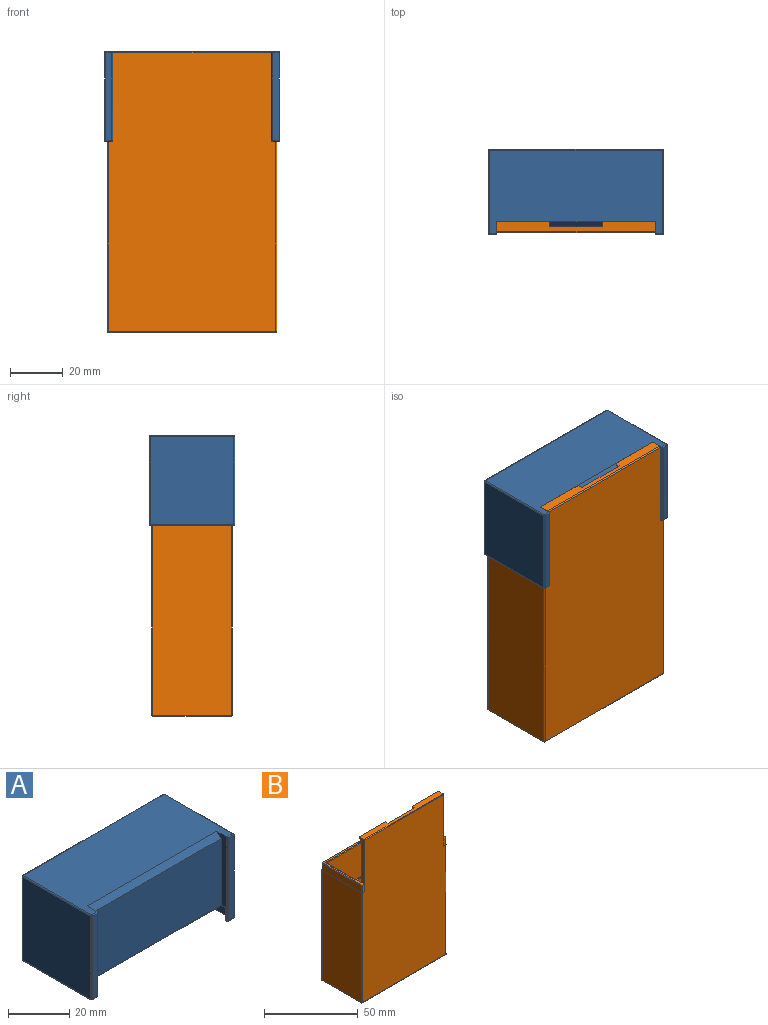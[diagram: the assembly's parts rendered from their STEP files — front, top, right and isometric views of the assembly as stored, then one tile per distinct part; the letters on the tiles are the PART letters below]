
ASSEMBLY  parts=2 mates=1
PART A: 63 faces, bbox 66x32.4x34 mm
  f0: plane 26.6x23mm, normal (1,0,0), area 611.8mm2, adj f1,f6,f19,f60
  f1: plane 60x26.6mm, normal (0,-1,0), area 1596mm2, adj f0,f2,f19,f59
  f2: plane 26.6x23mm, normal (-1,0,0), area 611.8mm2, adj f1,f6,f19,f61
  f3: plane 33.6x4.6mm, normal (1,0,0), area 77.4mm2, adj f4,f20,f21,f39,f43,f51,f57
  f4: plane 60x26.6mm, normal (0,-1,0), area 1596mm2, adj f3,f5,f21,f34
  f5: plane 33.6x4.6mm, normal (-1,0,0), area 77.4mm2, adj f4,f20,f21,f22,f26,f29,f30
  f6: plane 60x26.6mm, normal (0,1,0), area 1596mm2, adj f0,f2,f19,f62
  f7: plane 64x30.4mm, normal (0,0,-1), area 352.6mm2, adj f8,f9,f10,f11,f12,f30,f34,f39
  f8: plane 30.4x4.6mm, normal (-1,0,0), area 139.8mm2, adj f7,f9,f12,f31
  f9: plane 64x4.6mm, normal (0,-1,0), area 294.4mm2, adj f7,f8,f10,f35
  f10: plane 30.4x4.6mm, normal (1,0,0), area 139.8mm2, adj f7,f9,f11,f40
  f11: plane 4.6x1.6mm, normal (0,1,0), area 7.4mm2, adj f7,f10,f43,f44
  f12: plane 4.6x1.6mm, normal (0,1,0), area 7.4mm2, adj f7,f8,f26,f27
  f13: plane 33.2x2.6mm, normal (0,-1,0), area 86.3mm2, adj f14,f24,f29,f33
  f14: plane 33.2x32mm, normal (1,0,0), area 1062.4mm2, adj f13,f28,f37,f38
  f15: plane 65.2x33.2mm, normal (0,1,0), area 2164.6mm2, adj f36,f37,f46,f47
  f16: plane 33.2x31.6mm, normal (-1,0,0), area 1049.1mm2, adj f45,f46,f53,f54
  f17: plane 33.2x2.2mm, normal (0,-1,0), area 73mm2, adj f52,f53,f57,f58
  f18: plane 65.2x31.6mm, normal (0,0,-1), area 26.4mm2, adj f22,f24,f27,f28,f31,f35,f36,f40
  f19: plane 60x23mm, normal (0,0,-1), area 1380mm2, adj f0,f1,f2,f6
  f20: plane 65.2x31.6mm, normal (0,0,1), area 1784.3mm2, adj f3,f5,f21,f33,f38,f47,f54,f58
  f21: plane 60x2mm, normal (0,-0.71,0.71), area 169.7mm2, adj f3,f4,f5,f20
  f22: cylinder r=0.4mm len=0.4mm, axis (0,1,0), area 0.1mm2, adj f5,f18,f23,f25
  f23: sphere r=0.4mm, area 0.3mm2, adj f22,f26,f27
  f24: cylinder r=0.4mm len=2.6mm, axis (-1,0,0), area 1.5mm2, adj f13,f18,f25,f28
  f25: sphere r=0.4mm, area 0.3mm2, adj f22,f24,f29
  f26: cylinder r=0.4mm len=5mm, axis (0,0,1), area 3mm2, adj f5,f12,f23,f30
  f27: cylinder r=0.4mm len=2mm, axis (1,0,0), area 1.1mm2, adj f12,f18,f23,f31
  f28: cylinder r=0.4mm len=32mm, axis (0,-1,0), area 20mm2, adj f14,f18,f24,f32
  f29: cylinder r=0.4mm len=33.6mm, axis (0,0,-1), area 21mm2, adj f5,f13,f25,f33
  f30: cylinder r=0.4mm len=2.8mm, axis (0,1,0), area 1.4mm2, adj f5,f7,f26,f34
  f31: cylinder r=0.4mm len=31.2mm, axis (0,1,0), area 19.3mm2, adj f8,f18,f27,f35
  f32: sphere r=0.4mm, area 0.3mm2, adj f28,f36,f37
  f33: cylinder r=0.4mm len=3mm, axis (1,0,0), area 1.7mm2, adj f13,f20,f29,f38
  f34: cylinder r=0.4mm len=60.8mm, axis (-1,0,0), area 37.9mm2, adj f4,f7,f30,f39
  f35: cylinder r=0.4mm len=64.8mm, axis (-1,0,0), area 40.4mm2, adj f9,f18,f31,f40
  f36: cylinder r=0.4mm len=65.2mm, axis (1,0,0), area 41mm2, adj f15,f18,f32,f41
  f37: cylinder r=0.4mm len=33.2mm, axis (0,0,1), area 20.9mm2, adj f14,f15,f32,f42
  f38: cylinder r=0.4mm len=32mm, axis (0,1,0), area 20mm2, adj f14,f20,f33,f42
  f39: cylinder r=0.4mm len=2.8mm, axis (0,-1,0), area 1.4mm2, adj f3,f7,f34,f43
  f40: cylinder r=0.4mm len=31.2mm, axis (0,-1,0), area 19.3mm2, adj f10,f18,f35,f44
  f41: sphere r=0.4mm, area 0.3mm2, adj f36,f45,f46
  f42: sphere r=0.4mm, area 0.3mm2, adj f37,f38,f47
  f43: cylinder r=0.4mm len=5mm, axis (0,0,1), area 3mm2, adj f3,f11,f39,f48
  f44: cylinder r=0.4mm len=2mm, axis (1,0,0), area 1.1mm2, adj f11,f18,f40,f48
  f45: cylinder r=0.4mm len=31.6mm, axis (0,1,0), area 19.9mm2, adj f16,f18,f41,f49
  f46: cylinder r=0.4mm len=33.2mm, axis (0,0,-1), area 20.9mm2, adj f15,f16,f41,f50
  f47: cylinder r=0.4mm len=65.2mm, axis (-1,0,0), area 41mm2, adj f15,f20,f42,f50
  f48: sphere r=0.4mm, area 0.3mm2, adj f43,f44,f51
  f49: sphere r=0.4mm, area 0.3mm2, adj f45,f52,f53
  f50: sphere r=0.4mm, area 0.3mm2, adj f46,f47,f54
  f51: cylinder r=0.4mm len=0.4mm, axis (0,-1,0), area 0.1mm2, adj f3,f18,f48,f55
  f52: cylinder r=0.4mm len=2.2mm, axis (-1,0,0), area 1.4mm2, adj f17,f18,f49,f55
  f53: cylinder r=0.4mm len=33.2mm, axis (0,0,1), area 20.9mm2, adj f16,f17,f49,f56
  f54: cylinder r=0.4mm len=31.6mm, axis (0,-1,0), area 19.9mm2, adj f16,f20,f50,f56
  f55: sphere r=0.4mm, area 0.3mm2, adj f51,f52,f57
  f56: sphere r=0.4mm, area 0.3mm2, adj f53,f54,f58
  f57: cylinder r=0.4mm len=33.6mm, axis (0,0,-1), area 21mm2, adj f3,f17,f55,f58
  f58: cylinder r=0.4mm len=2.6mm, axis (1,0,0), area 1.5mm2, adj f17,f20,f56,f57
  f59: cylinder r=0.4mm len=60.8mm, axis (-1,0,0), area 37.9mm2, adj f1,f7,f60,f61
  f60: cylinder r=0.4mm len=23.8mm, axis (0,-1,0), area 14.6mm2, adj f0,f7,f59,f62
  f61: cylinder r=0.4mm len=23.8mm, axis (0,1,0), area 14.6mm2, adj f2,f7,f59,f62
  f62: cylinder r=0.4mm len=60.8mm, axis (1,0,0), area 37.9mm2, adj f6,f7,f60,f61
PART B: 61 faces, bbox 64x30.4x106 mm
  f0: plane 63x29.4mm, normal (0,0,1), area 172mm2, adj f7,f8,f13,f19,f20,f32,f35,f38
  f1: plane 105.2x63.2mm, normal (0,-1,0), area 6541.1mm2, adj f19,f20,f28,f44,f47,f52,f53
  f2: plane 29.4x4.6mm, normal (-1,0,0), area 135.2mm2, adj f28,f37,f40,f43
  f3: plane 29.4x4.6mm, normal (1,0,0), area 135.2mm2, adj f28,f31,f34,f35
  f4: plane 63x4.6mm, normal (0,1,0), area 289.8mm2, adj f28,f34,f37,f38
  f5: plane 71.6x29.6mm, normal (-1,0,0), area 2119.4mm2, adj f28,f45,f46,f47
  f6: plane 104x60mm, normal (0,1,0), area 6055mm2, adj f7,f8,f9,f19,f20,f21,f22,f23
  f7: plane 68x3.4mm, normal (1,0,0), area 231.2mm2, adj f0,f6,f13,f27
  f8: plane 68x3.4mm, normal (-1,0,0), area 231.2mm2, adj f0,f6,f13,f26
  f9: plane 30x3.4mm, normal (0,0,1), area 102mm2, adj f6,f13,f26,f27
  f10: plane 74.6x60mm, normal (0,1,0), area 4476mm2, adj f11,f16,f17,f59
  f11: plane 74.6x22mm, normal (1,0,0), area 1641.2mm2, adj f10,f12,f17,f57
  f12: plane 74.6x60mm, normal (0,-1,0), area 4476mm2, adj f11,f16,f17,f58
  f13: plane 75x60mm, normal (0,-1,0), area 4395mm2, adj f0,f7,f8,f9,f26,f27
  f14: plane 71.6x29.6mm, normal (1,0,0), area 2119.4mm2, adj f28,f50,f53,f56
  f15: plane 71.6x63.2mm, normal (0,1,0), area 4525.1mm2, adj f28,f45,f50,f51
  f16: plane 74.6x22mm, normal (-1,0,0), area 1641.2mm2, adj f10,f12,f17,f60
  f17: plane 60x22mm, normal (0,0,1), area 1320mm2, adj f10,f11,f12,f16
  f18: plane 63.2x29.6mm, normal (0,0,-1), area 1870.7mm2, adj f46,f51,f52,f56
  f19: plane 34x4mm, normal (-1,0,0), area 60.5mm2, adj f0,f1,f6,f21,f24,f28,f30,f41
  f20: plane 34x4mm, normal (1,0,0), area 60.5mm2, adj f0,f1,f6,f21,f25,f28,f29,f32
  f21: plane 60x3.6mm, normal (0,0,1), area 176mm2, adj f6,f19,f20,f22,f23,f24,f25,f44
  f22: plane 2x2mm, normal (-1,0,0), area 2mm2, adj f6,f21,f25
  f23: plane 2x2mm, normal (1,0,0), area 2mm2, adj f6,f21,f24
  f24: plane 20x2mm, normal (0,0.71,-0.71), area 56.6mm2, adj f6,f19,f21,f23
  f25: plane 20x2mm, normal (0,0.71,-0.71), area 56.6mm2, adj f6,f20,f21,f22
  f26: plane 15x7mm, normal (-0.42,0,0.91), area 56.3mm2, adj f6,f8,f9,f13
  f27: plane 15x7mm, normal (0.42,0,0.91), area 56.3mm2, adj f6,f7,f9,f13
  f28: plane 64x30.4mm, normal (0,0,1), area 12.8mm2, adj f1,f2,f3,f4,f5,f14,f15,f19
  f29: plane 4.6x1.5mm, normal (0,-1,0), area 6.9mm2, adj f20,f28,f31,f32
  f30: plane 4.6x1.5mm, normal (0,-1,0), area 6.9mm2, adj f19,f28,f41,f43
  f31: cylinder r=0.4mm len=4.6mm, axis (0,0,-1), area 2.9mm2, adj f3,f28,f29,f33
  f32: cylinder r=0.4mm len=1.5mm, axis (1,0,0), area 0.9mm2, adj f0,f20,f29,f33
  f33: sphere r=0.4mm, area 0.3mm2, adj f31,f32,f35
  f34: cylinder r=0.4mm len=4.6mm, axis (0,0,-1), area 2.9mm2, adj f3,f4,f28,f36
  f35: cylinder r=0.4mm len=29.4mm, axis (0,-1,0), area 18.5mm2, adj f0,f3,f33,f36
  f36: sphere r=0.4mm, area 0.3mm2, adj f34,f35,f38
  f37: cylinder r=0.4mm len=4.6mm, axis (0,0,1), area 2.9mm2, adj f2,f4,f28,f39
  f38: cylinder r=0.4mm len=63mm, axis (1,0,0), area 39.6mm2, adj f0,f4,f36,f39
  f39: sphere r=0.4mm, area 0.3mm2, adj f37,f38,f40
  f40: cylinder r=0.4mm len=29.4mm, axis (0,-1,0), area 18.5mm2, adj f0,f2,f39,f42
  f41: cylinder r=0.4mm len=1.5mm, axis (1,0,0), area 0.9mm2, adj f0,f19,f30,f42
  f42: sphere r=0.4mm, area 0.3mm2, adj f40,f41,f43
  f43: cylinder r=0.4mm len=4.6mm, axis (0,0,1), area 2.9mm2, adj f2,f28,f30,f42
  f44: cylinder r=0.4mm len=60mm, axis (-1,0,0), area 37.7mm2, adj f1,f19,f20,f21
  f45: cylinder r=0.4mm len=71.6mm, axis (0,0,1), area 45mm2, adj f5,f15,f28,f48
  f46: cylinder r=0.4mm len=29.6mm, axis (0,-1,0), area 18.6mm2, adj f5,f18,f48,f49
  f47: cylinder r=0.4mm len=71.6mm, axis (0,0,-1), area 45mm2, adj f1,f5,f28,f49
  f48: sphere r=0.4mm, area 0.3mm2, adj f45,f46,f51
  f49: sphere r=0.4mm, area 0.3mm2, adj f46,f47,f52
  f50: cylinder r=0.4mm len=71.6mm, axis (0,0,-1), area 45mm2, adj f14,f15,f28,f54
  f51: cylinder r=0.4mm len=63.2mm, axis (-1,0,0), area 39.7mm2, adj f15,f18,f48,f54
  f52: cylinder r=0.4mm len=63.2mm, axis (1,0,0), area 39.7mm2, adj f1,f18,f49,f55
  f53: cylinder r=0.4mm len=71.6mm, axis (0,0,1), area 45mm2, adj f1,f14,f28,f55
  f54: sphere r=0.4mm, area 0.3mm2, adj f50,f51,f56
  f55: sphere r=0.4mm, area 0.3mm2, adj f52,f53,f56
  f56: cylinder r=0.4mm len=29.6mm, axis (0,1,0), area 18.6mm2, adj f14,f18,f54,f55
  f57: cylinder r=0.4mm len=22.8mm, axis (0,-1,0), area 14mm2, adj f0,f11,f58,f59
  f58: cylinder r=0.4mm len=60.8mm, axis (-1,0,0), area 37.9mm2, adj f0,f12,f57,f60
  f59: cylinder r=0.4mm len=60.8mm, axis (1,0,0), area 37.9mm2, adj f0,f10,f57,f60
  f60: cylinder r=0.4mm len=22.8mm, axis (0,1,0), area 14mm2, adj f0,f16,f58,f59
PLACE A rot(axis=(0,0,-1),0deg) t=(-126.96,37.73,-27.11)mm
PLACE B t=(-126.1,0.35,-129.11)mm
MATE slider A.f20 <-> B.f18  axis (0,0,1) through (-117.39,17.82,-25.11)mm
